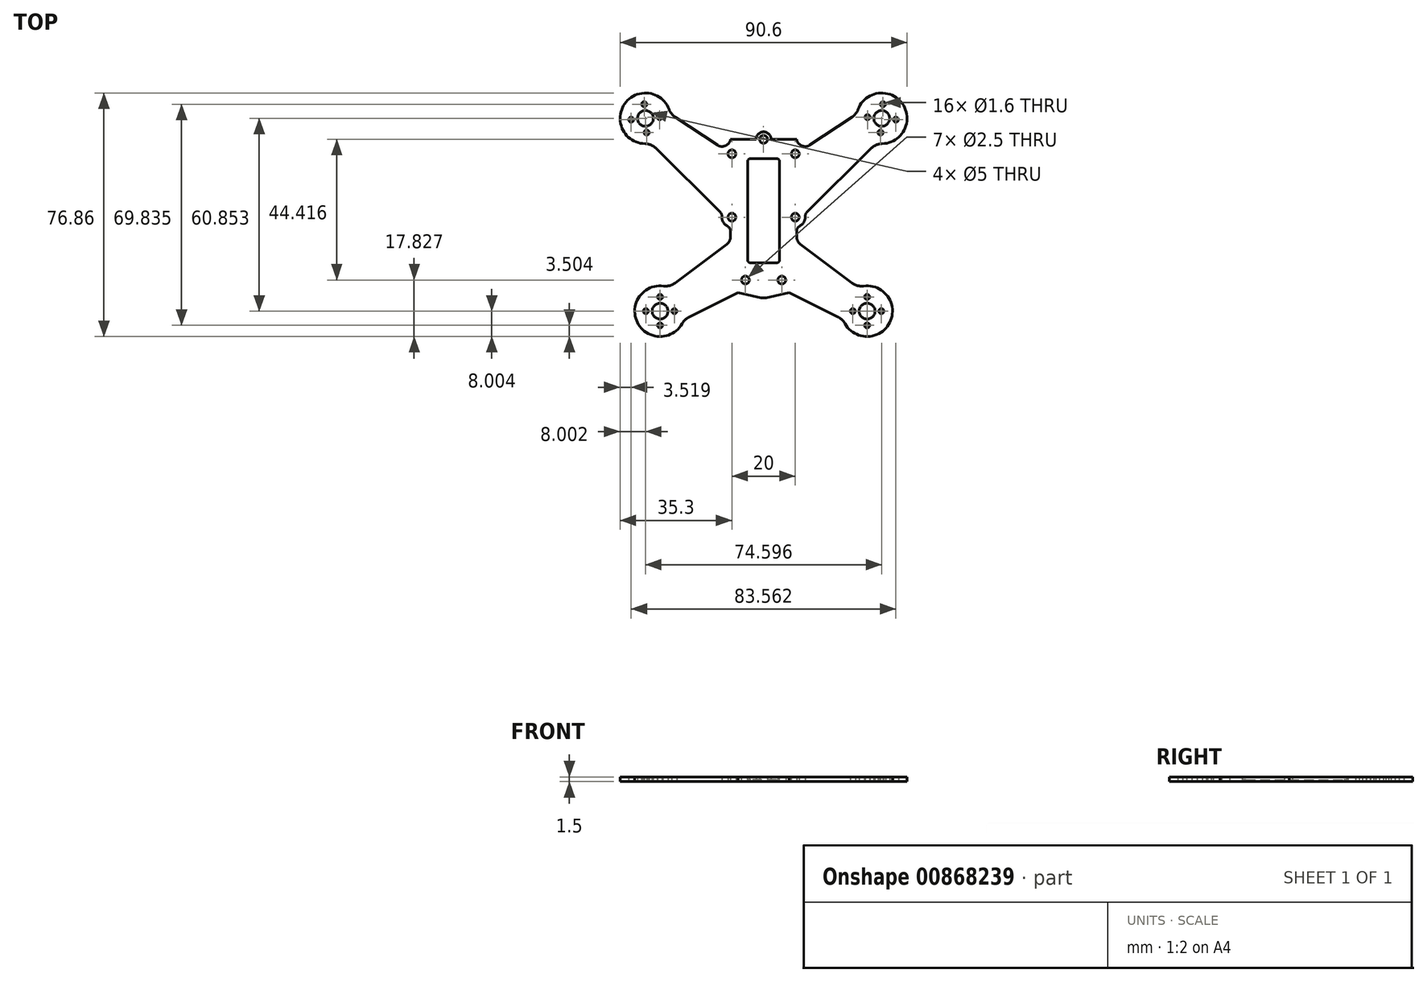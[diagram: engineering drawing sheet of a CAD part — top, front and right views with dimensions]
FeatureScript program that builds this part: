
annotation { "Feature Type Name" : "Feature", "Feature Type Description" : "" }
export const myFeature = defineFeature(function(context is Context, id is Id, definition is map)
    precondition{}
    {
        {
            var Q0;
            Q0=qCreatedBy(makeId("Top.planeOp"),FACE);
            var sketch = newSketch(context, id + "F0", { "sketchPlane" : qUnion([Q0])});
            skLineSegment(sketch, "E0.bottom", {"start": v(10, -10) * mm, "end": v(-10, -10) * mm, "construction": true});
            skLineSegment(sketch, "E0.top", {"start": v(10, 10) * mm, "end": v(-10, 10) * mm, "construction": true});
            skLineSegment(sketch, "E0.right", {"start": v(-10, -10) * mm, "end": v(-10, 10) * mm, "construction": true});
            skPoint(sketch, "E0.middle", {"position": v(0, 0) * mm});
            skCircle(sketch, "E1", {"center": v(-10, 10) * mm, "radius": 1.25 * mm});
            skCircle(sketch, "E2.MirrorC", {"center": v(-10, -10) * mm, "radius": 1.25 * mm});
            skLineSegment(sketch, "E3.MirrorCS", {"start": v(-13.73, -8.33) * mm, "end": v(-31.72, 9.52) * mm});
            skLineSegment(sketch, "E4", {"start": v(-9.22, 14.58) * mm, "end": v(-2.35, 14.58) * mm});
            skLineSegment(sketch, "E5.MirrorCS", {"start": v(9.22, 14.58) * mm, "end": v(2.35, 14.58) * mm});
            skArc(sketch, "E6.0", {"start": v(-11.49, -12.78) * mm, "mid": v(-12.77, -11.5) * mm, "end": v(-13.14, -9.74) * mm});
            skLineSegment(sketch, "E7", {"start": v(-10.43, -16.13) * mm, "end": v(-10.43, -14.54) * mm});
            skPoint(sketch, "E8.MirrorCS.start.orphan", {"position": v(-24.23, 18.37) * mm});
            skLineSegment(sketch, "E9", {"start": v(-24.3, 19.23) * mm, "end": v(-14.6, 12.77) * mm});
            skPoint(sketch, "E10.visualSharp", {"position": v(-13.05, -9) * mm});
            skArc(sketch, "E10.filletArc", {"start": v(-13.14, -9.74) * mm, "mid": v(-13.3, -8.97) * mm, "end": v(-13.73, -8.33) * mm});
            skPoint(sketch, "E11.visualSharp", {"position": v(-10.15, -12.87) * mm});
            skArc(sketch, "E11.filletArc", {"start": v(-10.43, -14.54) * mm, "mid": v(-10.71, -13.51) * mm, "end": v(-11.49, -12.78) * mm});
            skPoint(sketch, "E12.end.orphan", {"position": v(-29.55, -30.49) * mm});
            skPoint(sketch, "E13.start.orphan", {"position": v(-29.55, -29.44) * mm});
            skLineSegment(sketch, "E14", {"start": v(-11.63, -18.53) * mm, "end": v(-15.5, -21.44) * mm});
            skPoint(sketch, "E15.start.orphan", {"position": v(-23.32, -38.32) * mm});
            skPoint(sketch, "E16.orphan", {"position": v(-10.43, -20.72) * mm});
            skArc(sketch, "E17.MirrorCS", {"start": v(12.07, 12.38) * mm, "mid": v(12.07, 12.37) * mm, "end": v(12.08, 12.37) * mm});
            skArc(sketch, "E18.MirrorCS", {"start": v(11.49, -12.78) * mm, "mid": v(12.77, -11.5) * mm, "end": v(13.14, -9.74) * mm});
            skArc(sketch, "E19.MirrorCS", {"start": v(10.43, -14.54) * mm, "mid": v(10.71, -13.51) * mm, "end": v(11.49, -12.78) * mm});
            skLineSegment(sketch, "E20.MirrorCS", {"start": v(10.43, -16.13) * mm, "end": v(10.43, -14.54) * mm});
            skCircle(sketch, "E21.MirrorC", {"center": v(10, -10) * mm, "radius": 1.25 * mm});
            skLineSegment(sketch, "E22.MirrorCS", {"start": v(11.63, -18.53) * mm, "end": v(27.9, -30.77) * mm});
            skPoint(sketch, "E23.MirrorP", {"position": v(23.32, -38.32) * mm});
            skPoint(sketch, "E24.MirrorP", {"position": v(13, -9) * mm});
            skLineSegment(sketch, "E25.MirrorCS", {"start": v(8.06, -33.79) * mm, "end": v(23.58, -41.57) * mm});
            skPoint(sketch, "E26.MirrorP", {"position": v(10.43, -13.12) * mm});
            skPoint(sketch, "E27.MirrorP", {"position": v(29.55, -29.44) * mm});
            skCircle(sketch, "E28.MirrorC", {"center": v(10, 10) * mm, "radius": 1.25 * mm});
            skPoint(sketch, "E29.MirrorP", {"position": v(10.43, -20.72) * mm});
            skLineSegment(sketch, "E30.MirrorCS", {"start": v(10, -10) * mm, "end": v(10, 10) * mm, "construction": true});
            skPoint(sketch, "E31.MirrorP", {"position": v(29.55, -30.49) * mm});
            skArc(sketch, "E32", {"start": v(-29.81, 24.02) * mm, "mid": v(-43.84, 25.8) * mm, "end": v(-37.41, 13.2) * mm});
            skLineSegment(sketch, "E33", {"start": v(-31.72, 9.52) * mm, "end": v(-33.96, 11.75) * mm});
            skLineSegment(sketch, "E34", {"start": v(-24.3, 19.23) * mm, "end": v(-27.9, 21.62) * mm});
            skPoint(sketch, "E35.visualSharp", {"position": v(-29.43, 22.63) * mm});
            skArc(sketch, "E35.filletArc", {"start": v(-29.81, 24.02) * mm, "mid": v(-29.05, 22.67) * mm, "end": v(-27.9, 21.62) * mm});
            skPoint(sketch, "E36.visualSharp", {"position": v(-35.6, 13.38) * mm});
            skArc(sketch, "E36.filletArc", {"start": v(-33.96, 11.75) * mm, "mid": v(-35.55, 12.8) * mm, "end": v(-37.41, 13.2) * mm});
            skArc(sketch, "E37", {"start": v(-31.59, -31.73) * mm, "mid": v(-39.84, -43.22) * mm, "end": v(-25.7, -43.58) * mm});
            skPoint(sketch, "E38.orphan", {"position": v(-29.55, -32) * mm});
            skPoint(sketch, "E39.orphan", {"position": v(-24.68, -42.12) * mm});
            skLineSegment(sketch, "E40", {"start": v(-15.5, -21.44) * mm, "end": v(-27.9, -30.77) * mm});
            skPoint(sketch, "E41.visualSharp", {"position": v(-29.8, -32.2) * mm});
            skArc(sketch, "E41.filletArc", {"start": v(-31.59, -31.73) * mm, "mid": v(-29.66, -31.61) * mm, "end": v(-27.9, -30.77) * mm});
            skPoint(sketch, "E42.visualSharp", {"position": v(-25.14, -42.34) * mm});
            skArc(sketch, "E42.filletArc", {"start": v(-23.58, -41.57) * mm, "mid": v(-24.8, -42.42) * mm, "end": v(-25.7, -43.58) * mm});
            skArc(sketch, "E43.MirrorCS", {"start": v(23.58, -41.57) * mm, "mid": v(24.8, -42.42) * mm, "end": v(25.7, -43.58) * mm});
            skArc(sketch, "E44.MirrorCS", {"start": v(31.59, -31.73) * mm, "mid": v(29.66, -31.61) * mm, "end": v(27.9, -30.77) * mm});
            skPoint(sketch, "E45.MirrorP", {"position": v(29.8, -32.2) * mm});
            skPoint(sketch, "E46.MirrorP", {"position": v(24.68, -42.12) * mm});
            skPoint(sketch, "E47.MirrorP", {"position": v(25.14, -42.34) * mm});
            skPoint(sketch, "E48.MirrorP", {"position": v(29.55, -32) * mm});
            skArc(sketch, "E49.MirrorCS", {"start": v(31.59, -31.73) * mm, "mid": v(39.84, -43.22) * mm, "end": v(25.7, -43.58) * mm});
            skLineSegment(sketch, "E50", {"start": v(-37.3, 21.2) * mm, "end": v(-32.02, 21.66) * mm, "construction": true});
            skLineSegment(sketch, "E51", {"start": v(-37.3, 21.2) * mm, "end": v(-37.78, 26.74) * mm, "construction": true});
            skLineSegment(sketch, "E52", {"start": v(-37.3, 21.2) * mm, "end": v(-40.76, 17.08) * mm, "construction": true});
            skCircle(sketch, "E53", {"center": v(-37.7, 25.68) * mm, "radius": 0.8 * mm});
            skCircle(sketch, "E54.MirrorC", {"center": v(-36.9, 16.71) * mm, "radius": 0.8 * mm});
            skLineSegment(sketch, "E55", {"start": v(-10.45, 14.57) * mm, "end": v(-9.22, 14.58) * mm});
            skLineSegment(sketch, "E56.MirrorCS", {"start": v(10.45, 14.57) * mm, "end": v(9.22, 14.58) * mm});
            skPoint(sketch, "E57.MirrorCS.end.orphan", {"position": v(9.22, 14.58) * mm});
            skCircle(sketch, "E58", {"center": v(-37.3, 21.2) * mm, "radius": 2.5 * mm});
            skCircle(sketch, "E59", {"center": v(-32.82, 21.59) * mm, "radius": 0.8 * mm});
            skCircle(sketch, "E60.MirrorC", {"center": v(-41.78, 20.8) * mm, "radius": 0.8 * mm});
            skCircle(sketch, "E61", {"center": v(-32.67, -39.66) * mm, "radius": 2.5 * mm});
            skCircle(sketch, "E62", {"center": v(32.67, -39.66) * mm, "radius": 2.5 * mm});
            skLineSegment(sketch, "E63", {"start": v(-32.67, -39.66) * mm, "end": v(-32.67, -34.57) * mm, "construction": true});
            skLineSegment(sketch, "E64", {"start": v(-32.67, -39.66) * mm, "end": v(-27.37, -39.66) * mm, "construction": true});
            skCircle(sketch, "E65", {"center": v(-32.67, -35.16) * mm, "radius": 0.8 * mm});
            skCircle(sketch, "E66", {"center": v(-28.17, -39.66) * mm, "radius": 0.8 * mm});
            skCircle(sketch, "E67.MirrorC", {"center": v(-37.17, -39.66) * mm, "radius": 0.8 * mm});
            skCircle(sketch, "E68.MirrorC", {"center": v(-32.67, -44.16) * mm, "radius": 0.8 * mm});
            skCircle(sketch, "E69.MirrorC", {"center": v(32.67, -35.16) * mm, "radius": 0.8 * mm});
            skCircle(sketch, "E70.MirrorC", {"center": v(28.17, -39.66) * mm, "radius": 0.8 * mm});
            skCircle(sketch, "E71.MirrorC", {"center": v(32.67, -44.16) * mm, "radius": 0.8 * mm});
            skCircle(sketch, "E72.MirrorC", {"center": v(37.17, -39.66) * mm, "radius": 0.8 * mm});
            skArc(sketch, "E73", {"start": v(2.35, 14.58) * mm, "mid": v(0, 16.94) * mm, "end": v(-2.35, 14.58) * mm});
            skCircle(sketch, "E74", {"center": v(0, 14.58) * mm, "radius": 1.25 * mm});
            skCircle(sketch, "E75", {"center": v(-5.75, -29.83) * mm, "radius": 1.25 * mm});
            skCircle(sketch, "E76.MirrorC", {"center": v(5.75, -29.83) * mm, "radius": 1.25 * mm});
            skCircle(sketch, "E77", {"center": v(-37.3, 21.2) * mm, "radius": 25.4 * mm, "construction": true});
            skLineSegment(sketch, "E78", {"start": v(-7.5, -32.9) * mm, "end": v(-7.5, -32.1) * mm});
            skLineSegment(sketch, "E79.MirrorCS", {"start": v(7.5, -32.9) * mm, "end": v(7.5, -32.1) * mm});
            skLineSegment(sketch, "E80", {"start": v(-7.5, -32.1) * mm, "end": v(-0.52, -33.32) * mm});
            skLineSegment(sketch, "E81.MirrorCS", {"start": v(7.5, -32.1) * mm, "end": v(0.52, -33.32) * mm});
            skLineSegment(sketch, "E82.MirrorCS", {"start": v(-8.06, -33.79) * mm, "end": v(-23.58, -41.57) * mm});
            skPoint(sketch, "E83.visualSharp", {"position": v(-10.43, -17.63) * mm});
            skArc(sketch, "E83.filletArc", {"start": v(-11.63, -18.53) * mm, "mid": v(-10.75, -17.47) * mm, "end": v(-10.43, -16.13) * mm});
            skPoint(sketch, "E84.visualSharp", {"position": v(10.43, -17.63) * mm});
            skArc(sketch, "E84.filletArc", {"start": v(10.43, -16.13) * mm, "mid": v(10.75, -17.47) * mm, "end": v(11.63, -18.53) * mm});
            skLineSegment(sketch, "E85.0", {"start": v(-37.3, 21.2) * mm, "end": v(-37.3, 21.2) * mm});
            skLineSegment(sketch, "E85.1", {"start": v(-37.3, 21.2) * mm, "end": v(-37.7, 25.68) * mm, "construction": true});
            skLineSegment(sketch, "E85.8", {"start": v(-37.3, 21.2) * mm, "end": v(-32.82, 21.59) * mm, "construction": true});
            skLineSegment(sketch, "E85.9", {"start": v(-37.3, 21.2) * mm, "end": v(-37.3, 21.2) * mm});
            skLineSegment(sketch, "E86.0", {"start": v(-24.23, 18.37) * mm, "end": v(-24.3, 19.23) * mm, "construction": true});
            skLineSegment(sketch, "E87.MirrorCS", {"start": v(24.23, 18.37) * mm, "end": v(24.3, 19.23) * mm, "construction": true});
            skLineSegment(sketch, "E88.MirrorCS", {"start": v(34.8, 21.41) * mm, "end": v(32.82, 21.59) * mm, "construction": true});
            skCircle(sketch, "E89.MirrorC", {"center": v(32.82, 21.59) * mm, "radius": 0.8 * mm});
            skLineSegment(sketch, "E90.MirrorCS", {"start": v(37.52, 23.69) * mm, "end": v(37.78, 26.74) * mm, "construction": true});
            skCircle(sketch, "E91.MirrorC", {"center": v(37.7, 25.68) * mm, "radius": 0.8 * mm});
            skArc(sketch, "E92.MirrorCS", {"start": v(29.81, 24.02) * mm, "mid": v(29.05, 22.67) * mm, "end": v(27.9, 21.62) * mm});
            skLineSegment(sketch, "E93.MirrorCS", {"start": v(37.52, 23.69) * mm, "end": v(37.7, 25.68) * mm, "construction": true});
            skLineSegment(sketch, "E94.MirrorCS", {"start": v(31.72, 9.52) * mm, "end": v(33.96, 11.75) * mm});
            skArc(sketch, "E95.MirrorCS", {"start": v(14, 12.39) * mm, "mid": v(14, 12.38) * mm, "end": v(14, 12.38) * mm});
            skLineSegment(sketch, "E96.MirrorCS", {"start": v(24.3, 19.23) * mm, "end": v(27.9, 21.62) * mm});
            skArc(sketch, "E97.MirrorCS", {"start": v(13.14, -9.74) * mm, "mid": v(13.3, -8.97) * mm, "end": v(13.73, -8.33) * mm});
            skLineSegment(sketch, "E98.MirrorCS", {"start": v(34.8, 21.41) * mm, "end": v(32.02, 21.66) * mm, "construction": true});
            skArc(sketch, "E99.MirrorCS", {"start": v(33.96, 11.75) * mm, "mid": v(35.55, 12.8) * mm, "end": v(37.41, 13.2) * mm});
            skCircle(sketch, "E100.MirrorC", {"center": v(41.78, 20.8) * mm, "radius": 0.8 * mm});
            skLineSegment(sketch, "E101.MirrorCS", {"start": v(37.3, 21.2) * mm, "end": v(37.3, 21.2) * mm});
            skCircle(sketch, "E102.MirrorC", {"center": v(37.3, 21.2) * mm, "radius": 2.5 * mm});
            skLineSegment(sketch, "E103.MirrorCS", {"start": v(38.9, 19.28) * mm, "end": v(40.76, 17.08) * mm, "construction": true});
            skCircle(sketch, "E104.MirrorC", {"center": v(36.9, 16.71) * mm, "radius": 0.8 * mm});
            skPoint(sketch, "E105.MirrorP", {"position": v(11.38, 12.4) * mm});
            skLineSegment(sketch, "E106.MirrorCS", {"start": v(13.73, -8.33) * mm, "end": v(31.72, 9.52) * mm});
            skPoint(sketch, "E107.MirrorP", {"position": v(29.43, 22.63) * mm});
            skArc(sketch, "E108.MirrorCS", {"start": v(29.81, 24.02) * mm, "mid": v(43.84, 25.8) * mm, "end": v(37.41, 13.2) * mm});
            skLineSegment(sketch, "E109.MirrorCS", {"start": v(24.3, 19.23) * mm, "end": v(14.6, 12.77) * mm});
            skPoint(sketch, "E110.MirrorP", {"position": v(35.6, 13.38) * mm});
            skPoint(sketch, "E111.MirrorP", {"position": v(24.23, 18.37) * mm});
            skArc(sketch, "E112.filletArc", {"start": v(-8.06, -33.79) * mm, "mid": v(-7.66, -33.42) * mm, "end": v(-7.5, -32.9) * mm});
            skPoint(sketch, "E113.visualSharp", {"position": v(7.5, -33.51) * mm});
            skArc(sketch, "E113.filletArc", {"start": v(7.5, -32.9) * mm, "mid": v(7.66, -33.42) * mm, "end": v(8.06, -33.79) * mm});
            skArc(sketch, "E114", {"start": v(-14.6, 12.77) * mm, "mid": v(-12.03, 12.54) * mm, "end": v(-10.45, 14.57) * mm});
            skArc(sketch, "E115.MirrorCS", {"start": v(14.6, 12.77) * mm, "mid": v(12.03, 12.54) * mm, "end": v(10.45, 14.57) * mm});
            skArc(sketch, "E116", {"start": v(-0.52, -33.32) * mm, "mid": v(0, -33.37) * mm, "end": v(0.52, -33.32) * mm});
            skLineSegment(sketch, "E117", {"start": v(-8.06, -33.79) * mm, "end": v(-0.8, -35.44) * mm});
            skLineSegment(sketch, "E118.MirrorCS", {"start": v(8.06, -33.79) * mm, "end": v(0.8, -35.44) * mm});
            skArc(sketch, "E119", {"start": v(-0.8, -35.44) * mm, "mid": v(0, -35.53) * mm, "end": v(0.8, -35.44) * mm});
            skSolve(sketch);
        }
        {
            var Q0;
            Q0 = qSketchRegion(id + "F0", true);
            extrude(context, id + "F1", {"entities" : qUnion([Q0]), "depth" : 1.5 * mm, "offsetDistance" : 25 * mm});
        }
        {
            var Q0;
            Q0=makeQuery(id+"F1.opExtrude","CAP_FACE",FACE,{"disambiguationData":[OSD([sQuery(id+"F0.wireOp",EDGE,"E1"),sQuery(id+"F0.wireOp",EDGE,"E2.MirrorC"),sQuery(id+"F0.wireOp",EDGE,"E3.MirrorCS"),sQuery(id+"F0.wireOp",EDGE,"y2kMFbMD-wnTY-mhPc-kwCZ-sKt3fqoIUqFz"),sQuery(id+"F0.wireOp",EDGE,"E4"),sQuery(id+"F0.wireOp",EDGE,"E5.MirrorCS"),sQuery(id+"F0.wireOp",EDGE,"E6.0"),sQuery(id+"F0.wireOp",EDGE,"E7"),sQuery(id+"F0.wireOp",EDGE,"E9"),sQuery(id+"F0.wireOp",EDGE,"ed4d77fd-84fb-4928-a1d0-8a354550a09f.trimOffspring"),sQuery(id+"F0.wireOp",EDGE,"YEjxuU8P-0PHR-4L44-biup-P4lCU32f1Yp8"),sQuery(id+"F0.wireOp",EDGE,"IfdP7u2G-7WNu-d5Pd-mNno-UFvdBjyRlwrV"),sQuery(id+"F0.wireOp",EDGE,"9A18AKU5-5RBr-2HmA-jAMI-RS1cFzclcWtK"),sQuery(id+"F0.wireOp",EDGE,"E10.filletArc"),sQuery(id+"F0.wireOp",EDGE,"E11.filletArc"),sQuery(id+"F0.wireOp",EDGE,"4749de15-741f-4b66-a1a9-10ee3537e2c1.filletArc"),sQuery(id+"F0.wireOp",EDGE,"o0ytwcpU-ITSA-RGLR-Qy4W-6Kf7eDOwxHPG"),sQuery(id+"F0.wireOp",EDGE,"Ie9nLQdu-EHsN-rsvf-d6rz-OG9IvDCICKCv"),sQuery(id+"F0.wireOp",EDGE,"E14"),sQuery(id+"F0.wireOp",EDGE,"E17.MirrorCS"),sQuery(id+"F0.wireOp",EDGE,"ae011ea5-53d1-4d48-87bb-62cb2d3f341b1.MirrorCS"),sQuery(id+"F0.wireOp",EDGE,"ae011ea5-53d1-4d48-87bb-62cb2d3f341b2.MirrorCS"),sQuery(id+"F0.wireOp",EDGE,"ae011ea5-53d1-4d48-87bb-62cb2d3f341b3.MirrorCS"),sQuery(id+"F0.wireOp",EDGE,"ae011ea5-53d1-4d48-87bb-62cb2d3f341b4.MirrorCS"),sQuery(id+"F0.wireOp",EDGE,"E18.MirrorCS"),sQuery(id+"F0.wireOp",EDGE,"E57.MirrorCS"),sQuery(id+"F0.wireOp",EDGE,"E19.MirrorCS"),sQuery(id+"F0.wireOp",EDGE,"ae011ea5-53d1-4d48-87bb-62cb2d3f341b9.MirrorCS"),sQuery(id+"F0.wireOp",EDGE,"E20.MirrorCS"),sQuery(id+"F0.wireOp",EDGE,"ae011ea5-53d1-4d48-87bb-62cb2d3f341b11.MirrorCS"),sQuery(id+"F0.wireOp",EDGE,"E21.MirrorC"),sQuery(id+"F0.wireOp",EDGE,"E22.MirrorCS"),sQuery(id+"F0.wireOp",EDGE,"E25.MirrorCS"),sQuery(id+"F0.wireOp",EDGE,"ae011ea5-53d1-4d48-87bb-62cb2d3f341b27.MirrorCS"),sQuery(id+"F0.wireOp",EDGE,"E28.MirrorC"),sQuery(id+"F0.wireOp",EDGE,"ae011ea5-53d1-4d48-87bb-62cb2d3f341b34.MirrorCS"),sQuery(id+"F0.wireOp",EDGE,"E32"),sQuery(id+"F0.wireOp",EDGE,"E33"),sQuery(id+"F0.wireOp",EDGE,"E34"),sQuery(id+"F0.wireOp",EDGE,"E35.filletArc"),sQuery(id+"F0.wireOp",EDGE,"E36.filletArc"),sQuery(id+"F0.wireOp",EDGE,"fa71466c-7f19-46f4-8bf1-049a13ac7da10.MirrorCS"),sQuery(id+"F0.wireOp",EDGE,"fa71466c-7f19-46f4-8bf1-049a13ac7da11.MirrorCS"),sQuery(id+"F0.wireOp",EDGE,"fa71466c-7f19-46f4-8bf1-049a13ac7da14.MirrorCS"),sQuery(id+"F0.wireOp",EDGE,"4d8a396c-b604-4867-837e-bcaae563823d0.MirrorCS"),sQuery(id+"F0.wireOp",EDGE,"8b9809d2-5932-4ecb-bb79-a83574d74a990.MirrorCS"),sQuery(id+"F0.wireOp",EDGE,"E37"),sQuery(id+"F0.wireOp",EDGE,"d98oIcFI-e9vz-Wsgu-3rW5-GPOeA7f3mYs9"),sQuery(id+"F0.wireOp",EDGE,"E40"),sQuery(id+"F0.wireOp",EDGE,"E41.filletArc"),sQuery(id+"F0.wireOp",EDGE,"E42.filletArc"),sQuery(id+"F0.wireOp",EDGE,"E43.MirrorCS"),sQuery(id+"F0.wireOp",EDGE,"E44.MirrorCS"),sQuery(id+"F0.wireOp",EDGE,"E49.MirrorCS"),sQuery(id+"F0.wireOp",EDGE,"qP0Q4RVt-s1N3-gLHk-EzB1-P685khKtz2wF"),sQuery(id+"F0.wireOp",EDGE,"7doKaqZh-862E-nB9n-45yi-jqpLuEafjtFS")])],"isStart":false});
            var sketch = newSketch(context, id + "F2", { "sketchPlane" : qUnion([Q0])});
            skLineSegment(sketch, "E120.bottom", {"start": v(4.05, -24.45) * mm, "end": v(-4.05, -24.45) * mm});
            skLineSegment(sketch, "E120.top", {"start": v(4.05, 8.54) * mm, "end": v(-4.05, 8.54) * mm});
            skLineSegment(sketch, "E120.left", {"start": v(5.05, -23.45) * mm, "end": v(5.05, 7.54) * mm});
            skLineSegment(sketch, "E120.right", {"start": v(-5.05, -23.45) * mm, "end": v(-5.05, 7.54) * mm});
            skPoint(sketch, "E120.middle", {"position": v(0, -7.96) * mm});
            skPoint(sketch, "E121.visualSharp", {"position": v(-5.05, 8.54) * mm});
            skArc(sketch, "E121.filletArc", {"start": v(-4.05, 8.54) * mm, "mid": v(-4.75, 8.25) * mm, "end": v(-5.05, 7.54) * mm});
            skPoint(sketch, "E122.visualSharp", {"position": v(5.05, 8.54) * mm});
            skArc(sketch, "E122.filletArc", {"start": v(5.05, 7.54) * mm, "mid": v(4.75, 8.25) * mm, "end": v(4.05, 8.54) * mm});
            skPoint(sketch, "E123.visualSharp", {"position": v(-5.05, -24.45) * mm});
            skArc(sketch, "E123.filletArc", {"start": v(-5.05, -23.45) * mm, "mid": v(-4.75, -24.16) * mm, "end": v(-4.05, -24.45) * mm});
            skPoint(sketch, "E124.visualSharp", {"position": v(5.05, -24.45) * mm});
            skArc(sketch, "E124.filletArc", {"start": v(4.05, -24.45) * mm, "mid": v(4.75, -24.16) * mm, "end": v(5.05, -23.45) * mm});
            skSolve(sketch);
        }
        {
            var Q0;
            Q0 = qSketchRegion(id + "F2", true);
            extrude(context, id + "F3", {"entities" : qUnion([Q0]), "operationType" : NewBodyOperationType.REMOVE, "oppositeDirection" : true, "depth" : 1 * mm, "offsetDistance" : 25 * mm});
        }
    });
